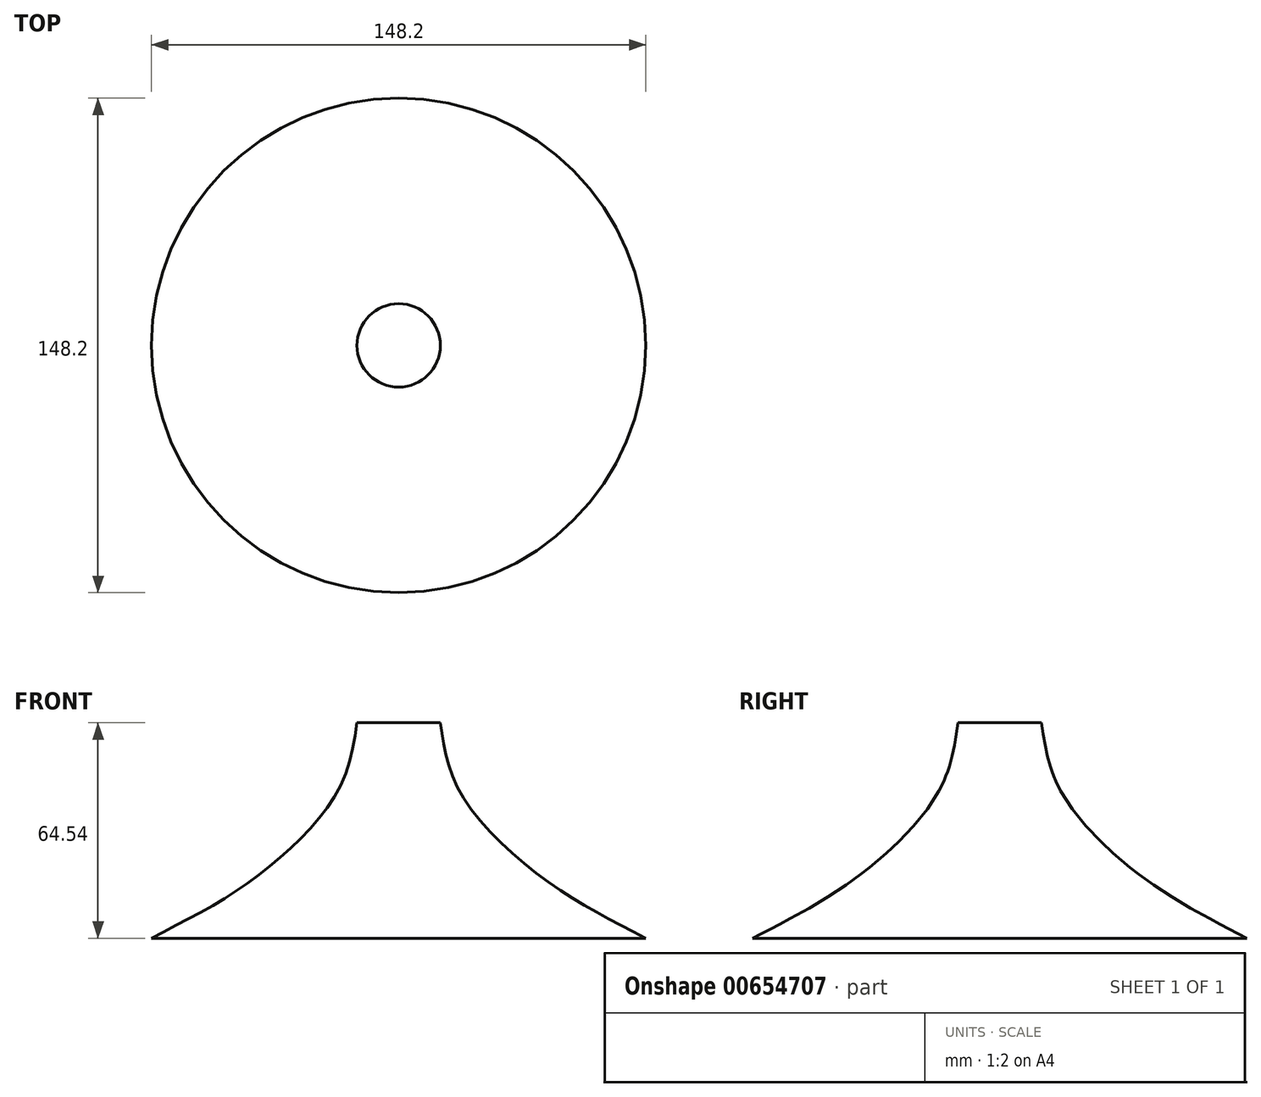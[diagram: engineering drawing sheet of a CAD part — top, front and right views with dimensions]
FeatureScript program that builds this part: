
annotation { "Feature Type Name" : "Feature", "Feature Type Description" : "" }
export const myFeature = defineFeature(function(context is Context, id is Id, definition is map)
    precondition{}
    {
        {
            var Q0;
            Q0=qCreatedBy(makeId("Top.planeOp"),FACE);
            var sketch = newSketch(context, id + "F0", { "sketchPlane" : qUnion([Q0])});
            skCircle(sketch, "E0", {"center": v(0, 0) * mm, "radius": 76.2 * mm});
            skSolve(sketch);
        }
        {
            var Q0;
            Q0=makeQuery(id+"F0.imprint","IMPRINT",FACE,{"disambiguationData":[TD([[makeQuery(id+"F0.imprint","IMPRINT",EDGE,{"derivedFrom":sQuery(id+"F0.wireOp",EDGE,"E0")}),1.0]])]});
            cPlane(context, id + "F1", {"entities" : qUnion([Q0]), "cplaneType" : CPlaneType.OFFSET, "offset" : 76.2 * mm, "width" : 150 * mm, "height" : 150 * mm});
        }
        {
            var Q0;
            Q0=qCreatedBy(makeId("Front.planeOp"),FACE);
            var sketch = newSketch(context, id + "F2", { "sketchPlane" : qUnion([Q0])});
            skFitSpline(sketch, "E1", {"points": [v(-74.1, 11.7) * mm, v(-44.5, 28.75) * mm, v(-18.33, 55.64) * mm, v(-12.5, 76.24) * mm], "startDerivative": vector(87.83, 45.78) * mm, "endDerivative": vector(11.06, 72.03) * mm});
            skLineSegment(sketch, "E2", {"start": v(0, 0) * mm, "end": v(0, 76.43) * mm});
            skSolve(sketch);
        }
        {
            var Q0;
            Q0 = qSketchRegion(id + "F2", true);
            var Q1;
            Q1=sQuery(id+"F2.wireOp",EDGE,"E1");
            var Q2;
            Q2=sQuery(id+"F2.wireOp",EDGE,"E2");
            revolve(context, id + "F3", {"bodyType" : ToolBodyType.SURFACE, "entities" : qUnion([Q0]), "surfaceEntities" : qUnion([Q1]), "axis" : qUnion([Q2]), "revolveType" : RevolveType.FULL});
        }
    });
